# Revit family: CENTUM Spannklauen Typ AF
name_source: partatom
category: HLS-Bauteile
revit_build: Autodesk Revit 2017 (Build: 20190507_1515(x64)
units: mm (PartAtom-declared; Revit-internal decimal feet)

## family parameters
Basisbauteil = Fläche
Beim Laden mit Abzugskörper schneiden = Nein
Bemaßung runder Anschluss = Durchmesser verwenden
Gemeinsam genutzt = Ja
Raumberechnungspunkt = Nein
Teiletyp = Normal

## types (4) — shared parameters
Fabrikat = MEFA
Festigkeitsklasse = 8.8
Firma = MEFA Befestigungs- und Montagesysteme GmbH
Kurztext1 = Spannklaue CENTUM AF
Material = sphärolitisches Gusseisen
Oberflaeche = feuerstückverzinkt
Vorgabe-Ansicht = 1219 mm
max. zul. Schublast = 0.00 kip

## per-type parameters (varying)
| type | Artikelnummer | Breite | EAN | Gewicht | Gewicht pro Bauteil | Kurztext2 | Länge | Typ | Werte im Brandfall vorhanden | benötigte Schraube | max Klemmdicke | max. zul. Last Zug | max. zul. Schublast, Träger verzinkt |
| CENTUM Spannklaue AF16 k | 1660004016/k | 49 mm | 4250928448972 | 0.43 kg | 0.43 kg | für Schraube M16 Klemmdicke 8 mm | 72 mm  [stored 0.23622 ft] | AF16 kurz |  | M16 | 0 mm  [stored 0 ft] | 3.60 kip | 10 kN |
| CENTUM Spannklaue AF16 | 1660004016 | 49 mm | 4250928437327 | 0.46 kg | 0.46 kg | für Schraube M16 Klemmdicke 15 mm | 72 mm  [stored 0.23622 ft] | AF16 mittel | 8 kN | M16 | 15 mm  [stored 0.0492126 ft] | 3.60 kip | 10 kN |
| CENTUM Spannklaue AF12 k | 1660004012/k | 39 mm  [stored 0.127953 ft] | 4250928448965 | 0.19 kg | 0.19 kg | für Schraube M12 Klemmdicke 5 mm | 56 mm  [stored 0.183727 ft] | AF12 kurz |  | M12 | 0 mm  [stored 0 ft] | 1.91 kip | 3,9 kN |
| CENTUM Spannklaue AF12 | 1660004012 | 39 mm  [stored 0.127953 ft] | 4250928437310 | 0.24 kg | 0.24 kg | für Schraube M12 Klemmdicke 12,5 mm | 56 mm  [stored 0.183727 ft] | AF12 mittel |  | M12 | 0 mm  [stored 0 ft] | 1.91 kip | 3,9 kN |

note: [stored X ft] marks values corroborated as IEEE doubles in the binary element streams (Revit-internal decimal feet)
